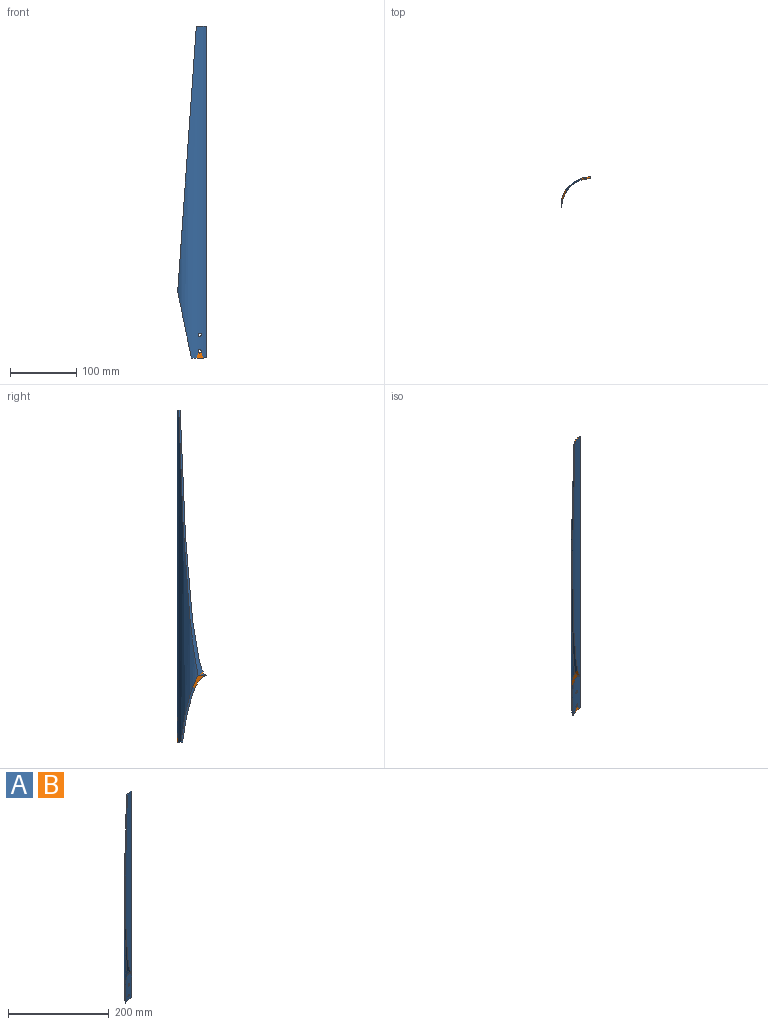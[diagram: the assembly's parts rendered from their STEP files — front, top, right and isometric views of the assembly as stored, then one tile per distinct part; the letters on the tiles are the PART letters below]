
ASSEMBLY  parts=2 mates=1
PART A: 9 faces, bbox 43x45x500 mm
  f0: cylinder r=45mm len=500mm, axis (0,0,-1), area 16859.5mm2, adj f2,f3,f4,f5,f6,f7,f8
  f1: cylinder r=43mm len=500mm, axis (0,0,-1), area 17295.5mm2, adj f2,f3,f4,f5,f6,f7,f8
  f2: plane 15x4.7mm, normal (0,0,1), area 30.6mm2, adj f0,f1,f4,f5
  f3: plane 22.5x8.36mm, normal (0,0,-1), area 47.2mm2, adj f0,f1,f4,f6
  f4: plane 500x2mm, normal (1,0,0), area 1000mm2, adj f0,f1,f2,f3
  f5: plane 400x42.43mm, normal (-1,0,0.07), area 1286.7mm2, adj f0,f1,f2,f6
  f6: plane 100x38.97mm, normal (-0.98,0,-0.2), area 364.6mm2, adj f0,f1,f3,f5
  f7: cylinder r=2.5mm len=5mm, axis (0,-1,0), area 32.3mm2, adj f0,f1
  f8: cylinder r=2.5mm len=5mm, axis (0,-1,0), area 32.3mm2, adj f0,f1
PART B: same geometry as A
PLACE A t=(0.87,-0.87,-47.89)mm
PLACE B t=(0.87,-0.87,-47.89)mm fixed
MATE fastened A.f0 <-> B.f0  axis (0,0,-1) through (0.87,-0.87,202.11)mm
